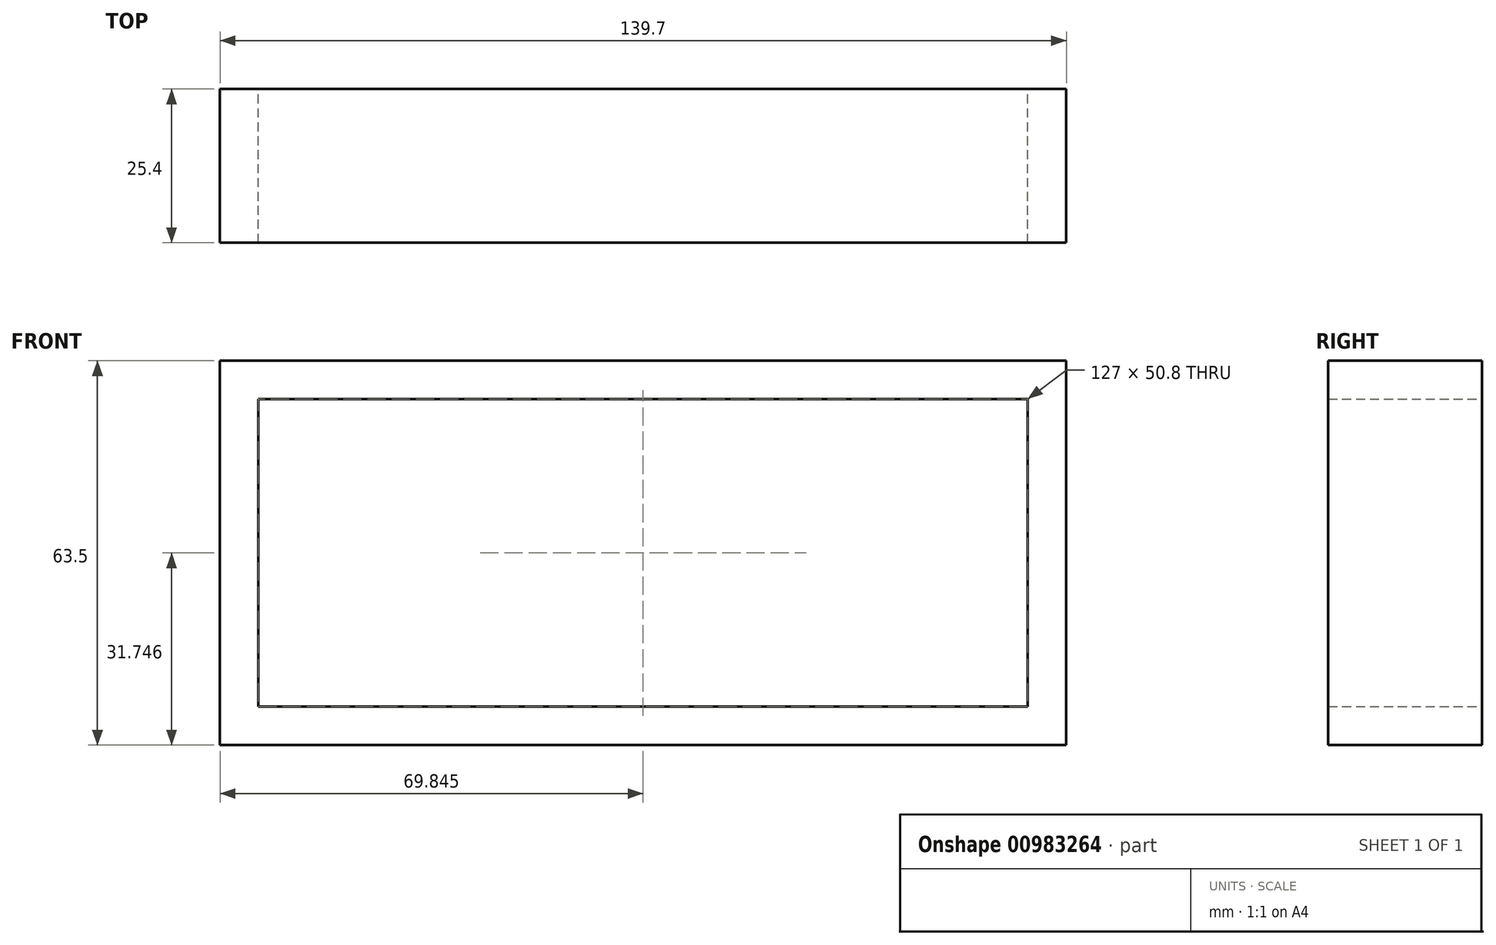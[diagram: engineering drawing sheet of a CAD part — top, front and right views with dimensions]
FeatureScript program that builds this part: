
annotation { "Feature Type Name" : "Feature", "Feature Type Description" : "" }
export const myFeature = defineFeature(function(context is Context, id is Id, definition is map)
    precondition{}
    {
        {
            var Q0;
            Q0=qCreatedBy(makeId("Front.planeOp"),FACE);
            var sketch = newSketch(context, id + "F0", { "sketchPlane" : qUnion([Q0])});
            skLineSegment(sketch, "E0.bottom", {"start": v(-114.73, -14.67) * mm, "end": v(12.27, -14.67) * mm});
            skLineSegment(sketch, "E0.top", {"start": v(-114.73, -65.47) * mm, "end": v(12.27, -65.47) * mm});
            skLineSegment(sketch, "E0.left", {"start": v(-114.73, -14.67) * mm, "end": v(-114.73, -65.47) * mm});
            skLineSegment(sketch, "E0.right", {"start": v(12.27, -14.67) * mm, "end": v(12.27, -65.47) * mm});
            skLineSegment(sketch, "E1.0", {"start": v(-121.08, -8.32) * mm, "end": v(-121.08, -71.82) * mm});
            skLineSegment(sketch, "E1.1", {"start": v(-121.08, -8.32) * mm, "end": v(18.62, -8.32) * mm});
            skLineSegment(sketch, "E1.2", {"start": v(18.62, -8.32) * mm, "end": v(18.62, -71.82) * mm});
            skLineSegment(sketch, "E1.3", {"start": v(-121.08, -71.82) * mm, "end": v(18.62, -71.82) * mm});
            skSolve(sketch);
        }
        {
            var Q0;
            Q0 = qSketchRegion(id + "F0", true);
            extrude(context, id + "F1", {"entities" : qUnion([Q0]), "depth" : 25.4 * mm, "offsetDistance" : 25.4 * mm});
        }
    });
